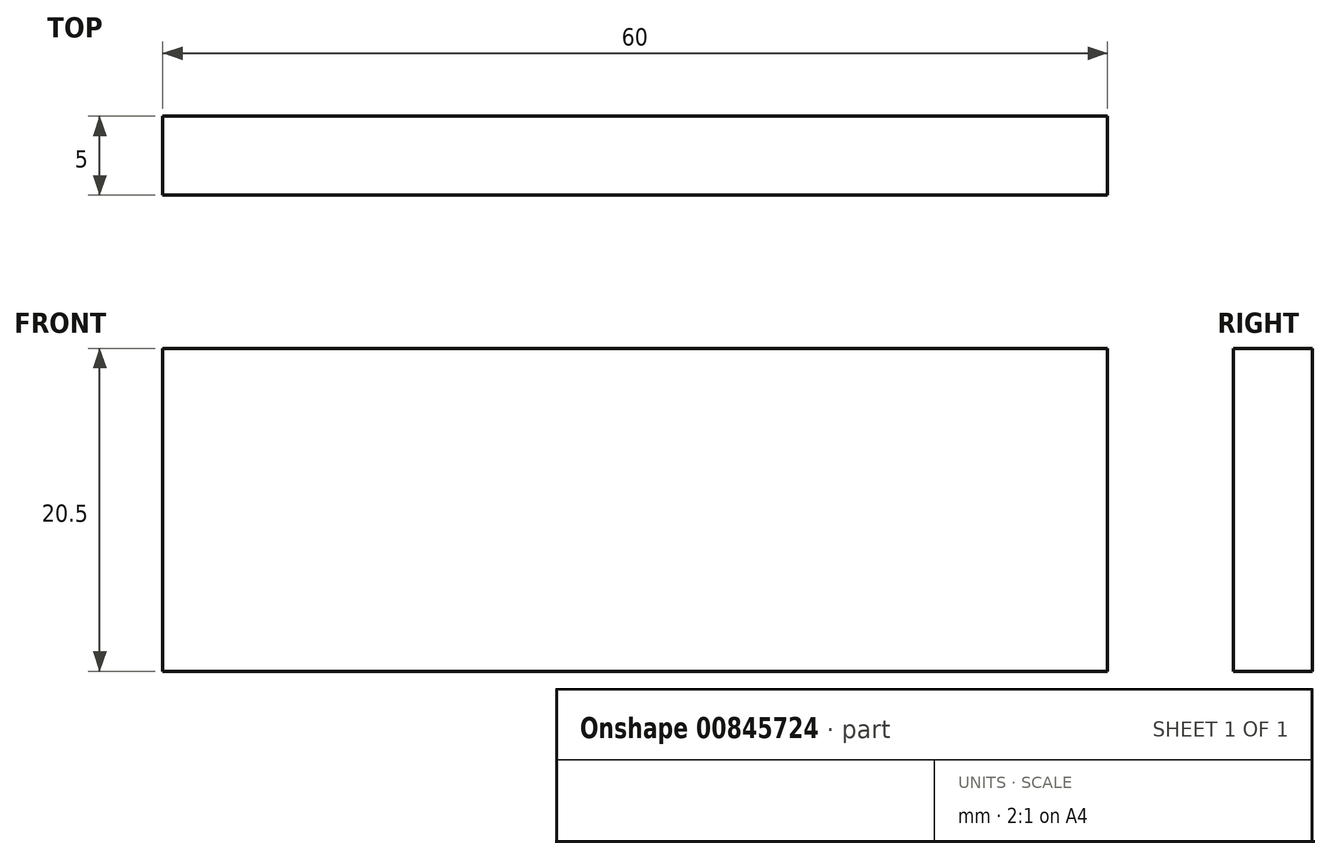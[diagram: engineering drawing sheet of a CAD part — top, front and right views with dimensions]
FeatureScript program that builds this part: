
annotation { "Feature Type Name" : "Feature", "Feature Type Description" : "" }
export const myFeature = defineFeature(function(context is Context, id is Id, definition is map)
    precondition{}
    {
        {
            var Q0;
            Q0=qCreatedBy(makeId("Right.planeOp"),FACE);
            var sketch = newSketch(context, id + "F0", { "sketchPlane" : qUnion([Q0])});
            skLineSegment(sketch, "E0", {"start": v(0, 0) * mm, "end": v(-5, 0) * mm});
            skLineSegment(sketch, "E1", {"start": v(0, 0) * mm, "end": v(0, 32.5) * mm});
            skLineSegment(sketch, "E2", {"start": v(-5, 32.5) * mm, "end": v(-5, 0) * mm});
            skLineSegment(sketch, "E3", {"start": v(-5, 32.5) * mm, "end": v(0, 32.5) * mm});
            skSolve(sketch);
        }
        {
            var Q0;
            Q0=makeQuery(id+"F0.imprint","IMPRINT",FACE,{"disambiguationData":[TD([[makeQuery(id+"F0.imprint","IMPRINT",EDGE,{"derivedFrom":sQuery(id+"F0.wireOp",EDGE,"E0")}),-1.0]])]});
            extrude(context, id + "F1", {"entities" : qUnion([Q0]), "depth" : 60 * mm, "offsetDistance" : 25 * mm});
        }
        {
            var Q0;
            Q0=qCreatedBy(makeId("Right.planeOp"),FACE);
            var sketch = newSketch(context, id + "F2", { "sketchPlane" : qUnion([Q0])});
            skLineSegment(sketch, "E4", {"start": v(0, 12) * mm, "end": v(0, 0) * mm});
            skLineSegment(sketch, "E5", {"start": v(0, 0) * mm, "end": v(0, 12) * mm});
            skLineSegment(sketch, "E6", {"start": v(0, 12) * mm, "end": v(-5, 12) * mm});
            skLineSegment(sketch, "E7", {"start": v(-5, 0) * mm, "end": v(0, 0) * mm});
            skLineSegment(sketch, "E8", {"start": v(-5, 0) * mm, "end": v(-5, 12) * mm});
            skSolve(sketch);
        }
        {
            var Q0;
            Q0=makeQuery(id+"F2.imprint","IMPRINT",FACE,{"disambiguationData":[TD([[makeQuery(id+"F2.imprint","IMPRINT",EDGE,{"derivedFrom":sQuery(id+"F2.wireOp",EDGE,"E4")}),-1.0]])]});
            extrude(context, id + "F3", {"entities" : qUnion([Q0]), "operationType" : NewBodyOperationType.REMOVE, "depth" : 60 * mm, "offsetDistance" : 25 * mm});
        }
    });
